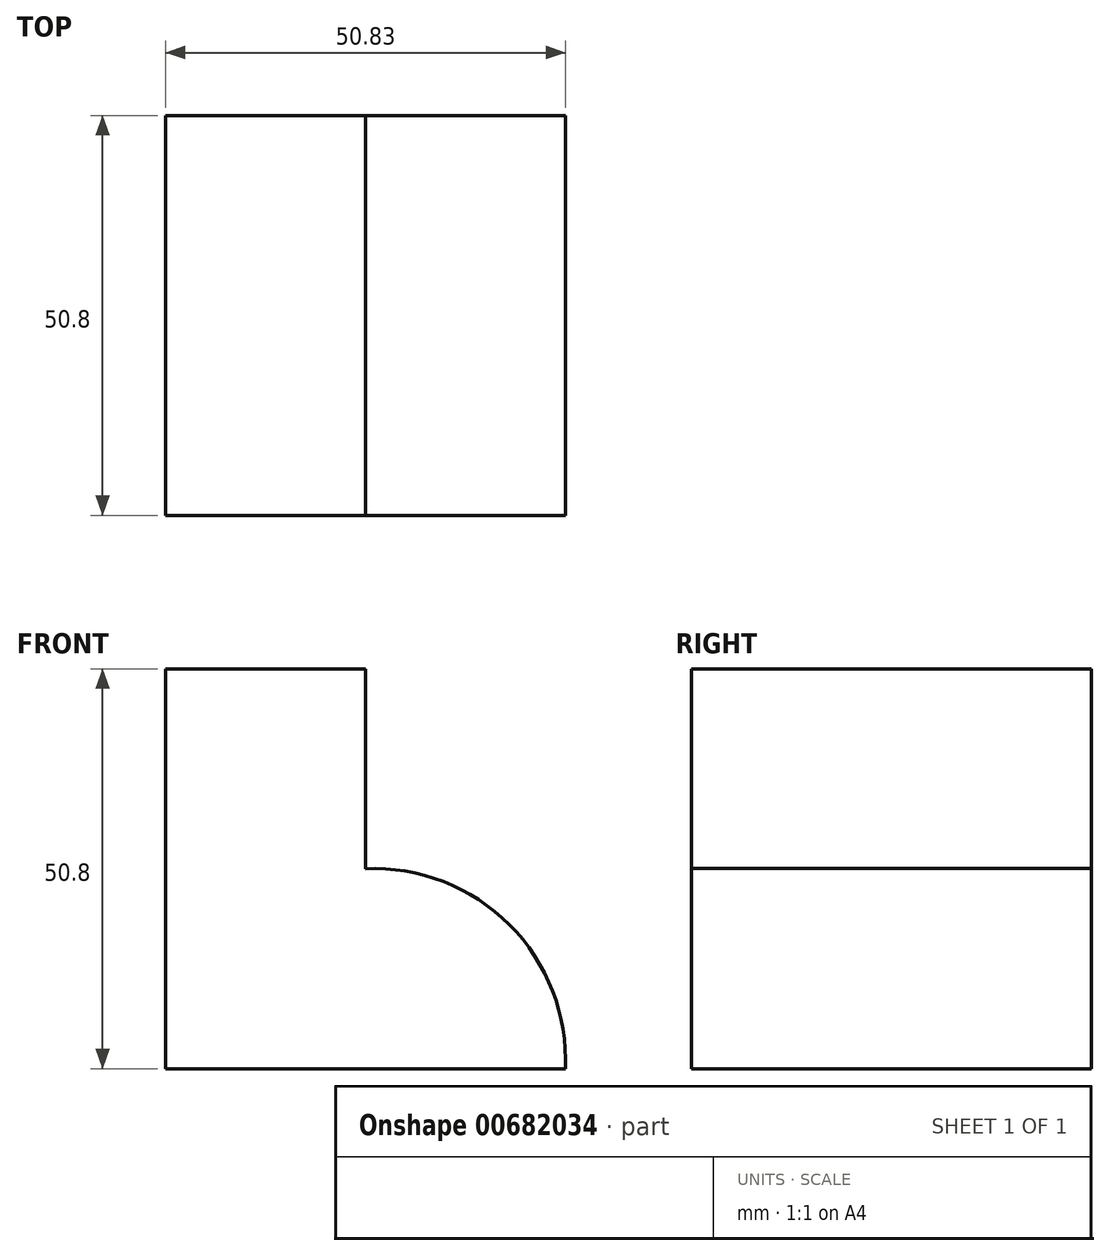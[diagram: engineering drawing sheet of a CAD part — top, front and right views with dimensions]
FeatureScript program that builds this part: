
annotation { "Feature Type Name" : "Feature", "Feature Type Description" : "" }
export const myFeature = defineFeature(function(context is Context, id is Id, definition is map)
    precondition{}
    {
        {
            var Q0;
            Q0=qCreatedBy(makeId("Front.planeOp"),FACE);
            var sketch = newSketch(context, id + "F0", { "sketchPlane" : qUnion([Q0])});
            skLineSegment(sketch, "E0", {"start": v(-54.33, 50.8) * mm, "end": v(-54.33, 0) * mm});
            skLineSegment(sketch, "E1", {"start": v(-54.33, 0) * mm, "end": v(-3.53, 0) * mm});
            skLineSegment(sketch, "E2", {"start": v(-54.33, 50.8) * mm, "end": v(-28.93, 50.8) * mm});
            skLineSegment(sketch, "E3", {"start": v(-28.93, 50.8) * mm, "end": v(-28.93, 25.4) * mm});
            skArc(sketch, "E4", {"start": v(-3.53, 0) * mm, "mid": v(-10.64, 18.28) * mm, "end": v(-28.93, 25.4) * mm});
            skSolve(sketch);
        }
        {
            var Q0;
            Q0 = qSketchRegion(id + "F0", true);
            extrude(context, id + "F1", {"entities" : qUnion([Q0]), "depth" : 50.8 * mm, "offsetDistance" : 25.4 * mm});
        }
    });
